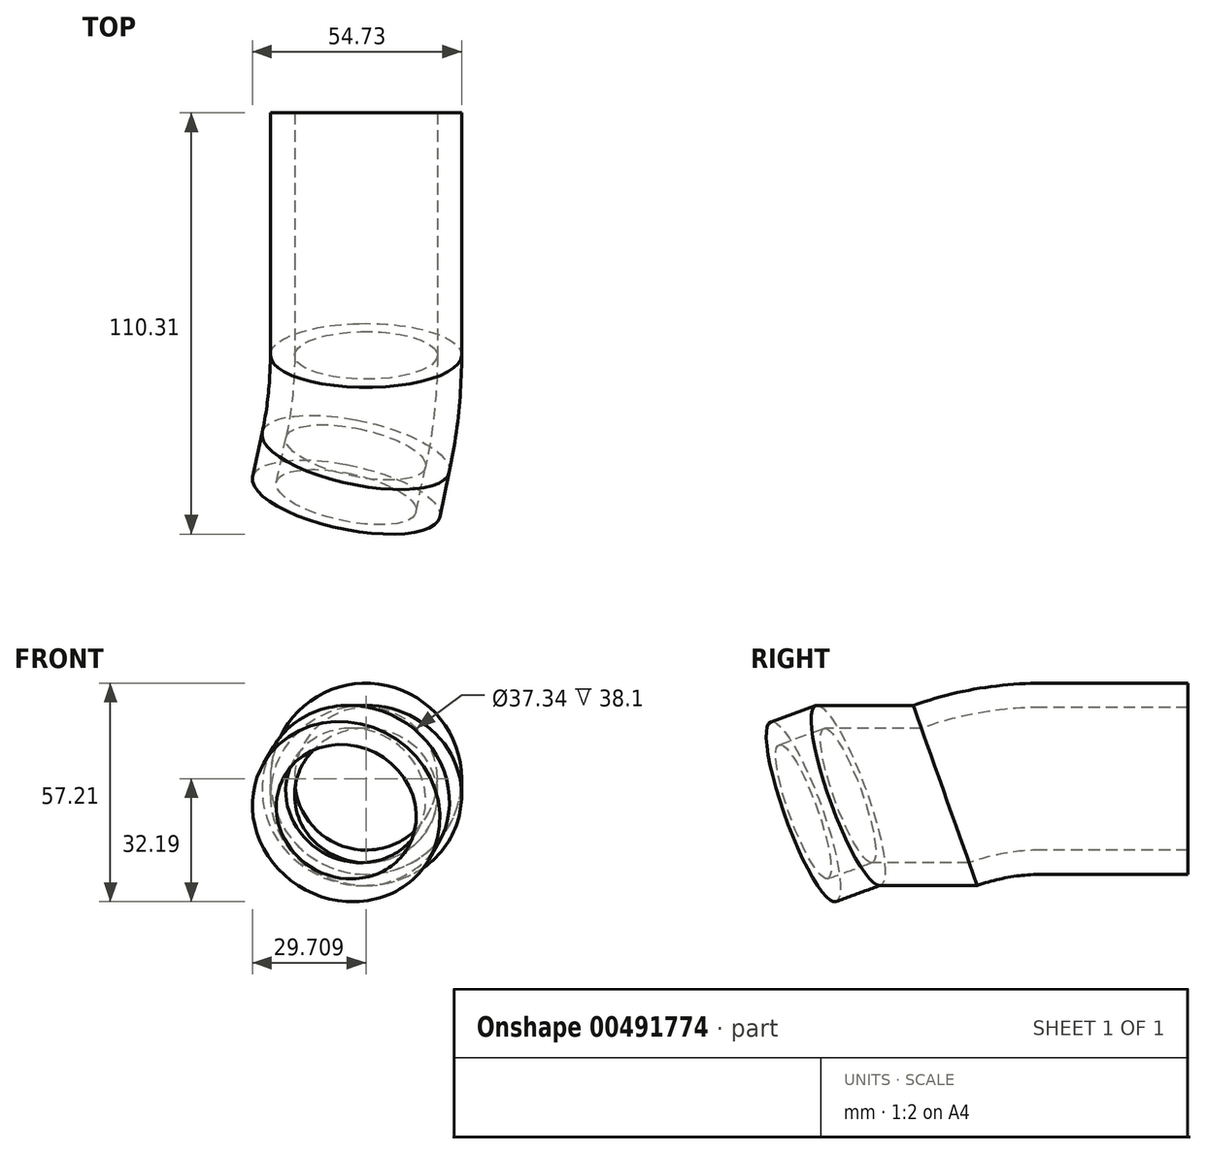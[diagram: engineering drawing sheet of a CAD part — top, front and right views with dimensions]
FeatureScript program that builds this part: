
annotation { "Feature Type Name" : "Feature", "Feature Type Description" : "" }
export const myFeature = defineFeature(function(context is Context, id is Id, definition is map)
    precondition{}
    {
        {
            var Q0;
            Q0=qCreatedBy(makeId("Right.planeOp"),FACE);
            var sketch = newSketch(context, id + "F0", { "sketchPlane" : qUnion([Q0])});
            skLineSegment(sketch, "E0", {"start": v(8.66, -23.88) * mm, "end": v(-8.66, 23.88) * mm, "construction": true});
            skSolve(sketch);
        }
        {
            var Q0;
            Q0=qCreatedBy(makeId("Top.planeOp"),FACE);
            var sketch = newSketch(context, id + "F1", { "sketchPlane" : qUnion([Q0])});
            skLineSegment(sketch, "E1", {"start": v(-24.84, 5.3) * mm, "end": v(24.84, -5.3) * mm, "construction": true});
            skSolve(sketch);
        }
        {
            var Q0;
            Q0=sQuery(id+"F0.wireOp",VERTEX,"E0.end");
            var Q1;
            Q1=sQuery(id+"F1.wireOp",VERTEX,"E1.end");
            var Q2;
            Q2=sQuery(id+"F1.wireOp",VERTEX,"E1.start");
            cPlane(context, id + "F2", {"entities" : qUnion([Q0, Q1, Q2]), "cplaneType" : CPlaneType.THREE_POINT, "offset" : 25.4 * mm, "width" : 152.4 * mm, "height" : 152.4 * mm});
        }
        {
            var Q0;
            Q0=qCreatedBy(id+"F2.planeOp",FACE);
            var sketch = newSketch(context, id + "F3", { "sketchPlane" : qUnion([Q0])});
            skCircle(sketch, "E2", {"center": v(0, 0) * mm, "radius": 18.67 * mm});
            skCircle(sketch, "E3", {"center": v(0, 0) * mm, "radius": 25.02 * mm});
            skSolve(sketch);
        }
        {
            var Q0;
            Q0=qCreatedBy(makeId("Top.planeOp"),FACE);
            var sketch = newSketch(context, id + "F4", { "sketchPlane" : qUnion([Q0])});
            skArc(sketch, "E4", {"start": v(0, 0) * mm, "mid": v(2, 12.63) * mm, "end": v(2.68, 25.4) * mm});
            skLineSegment(sketch, "E5", {"start": v(2.68, 25.4) * mm, "end": v(2.68, 50.8) * mm, "construction": true});
            skLineSegment(sketch, "E6.0", {"start": v(-24.84, 5.3) * mm, "end": v(24.84, -5.3) * mm, "construction": true});
            skLineSegment(sketch, "E7", {"start": v(-24.84, 5.3) * mm, "end": v(-119.09, 25.4) * mm, "construction": true});
            skSolve(sketch);
        }
        {
            var Q0;
            Q0=makeQuery(id+"F3.imprint","IMPRINT",FACE,{"disambiguationData":[TD([[makeQuery(id+"F3.imprint","IMPRINT",EDGE,{"derivedFrom":sQuery(id+"F3.wireOp",EDGE,"E2")}),-1.0]])]});
            var Q1;
            Q1=sQuery(id+"F4.wireOp",EDGE,"E4");
            sweep(context, id + "F5", {"profiles" : qUnion([Q0]), "path" : qUnion([Q1])});
        }
        {
            var Q0;
            Q0=qCreatedBy(makeId("Right.planeOp"),FACE);
            var sketch = newSketch(context, id + "F6", { "sketchPlane" : qUnion([Q0])});
            skLineSegment(sketch, "E8.0", {"start": v(17.04, 23.58) * mm, "end": v(33.76, -23.58) * mm});
            skArc(sketch, "E9", {"start": v(25.4, 0) * mm, "mid": v(37.91, 3.27) * mm, "end": v(50.8, 4.37) * mm});
            skLineSegment(sketch, "E10", {"start": v(50.8, 4.37) * mm, "end": v(76.2, 4.37) * mm, "construction": true});
            skLineSegment(sketch, "E11", {"start": v(33.76, -23.58) * mm, "end": v(50.8, -71.63) * mm, "construction": true});
            skSolve(sketch);
        }
        {
            var Q0;
            Q0=makeQuery(id+"F5.opSweep","CAP_FACE",FACE,{"disambiguationData":[OSD([sQuery(id+"F3.wireOp",EDGE,"E2"),sQuery(id+"F3.wireOp",EDGE,"E3"),sQuery(id+"F4.wireOp",VERTEX,"E4.end")])],"isStart":false});
            var Q1;
            Q1=sQuery(id+"F6.wireOp",EDGE,"E9");
            sweep(context, id + "F7", {"operationType" : NewBodyOperationType.ADD, "profiles" : qUnion([Q0]), "path" : qUnion([Q1])});
        }
        {
            var Q0;
            Q0=makeQuery(id+"F5.opSweep","CAP_FACE",FACE,{"disambiguationData":[OSD([sQuery(id+"F3.wireOp",EDGE,"E2"),sQuery(id+"F3.wireOp",EDGE,"E3"),sQuery(id+"F4.wireOp",VERTEX,"E4.start")])],"isStart":true});
            extrude(context, id + "F8", {"entities" : qUnion([Q0]), "operationType" : NewBodyOperationType.ADD, "depth" : 12.7 * mm});
        }
        {
            var Q0;
            Q0=makeQuery(id+"F7.opSweep","CAP_FACE",FACE,{"disambiguationData":[OSD([sQuery(id+"F3.wireOp",EDGE,"E2"),sQuery(id+"F3.wireOp",EDGE,"E3"),sQuery(id+"F4.wireOp",VERTEX,"E4.end"),sQuery(id+"F6.wireOp",VERTEX,"E9.end")])],"isStart":false});
            extrude(context, id + "F9", {"entities" : qUnion([Q0]), "operationType" : NewBodyOperationType.ADD, "depth" : 38.1 * mm});
        }
    });
